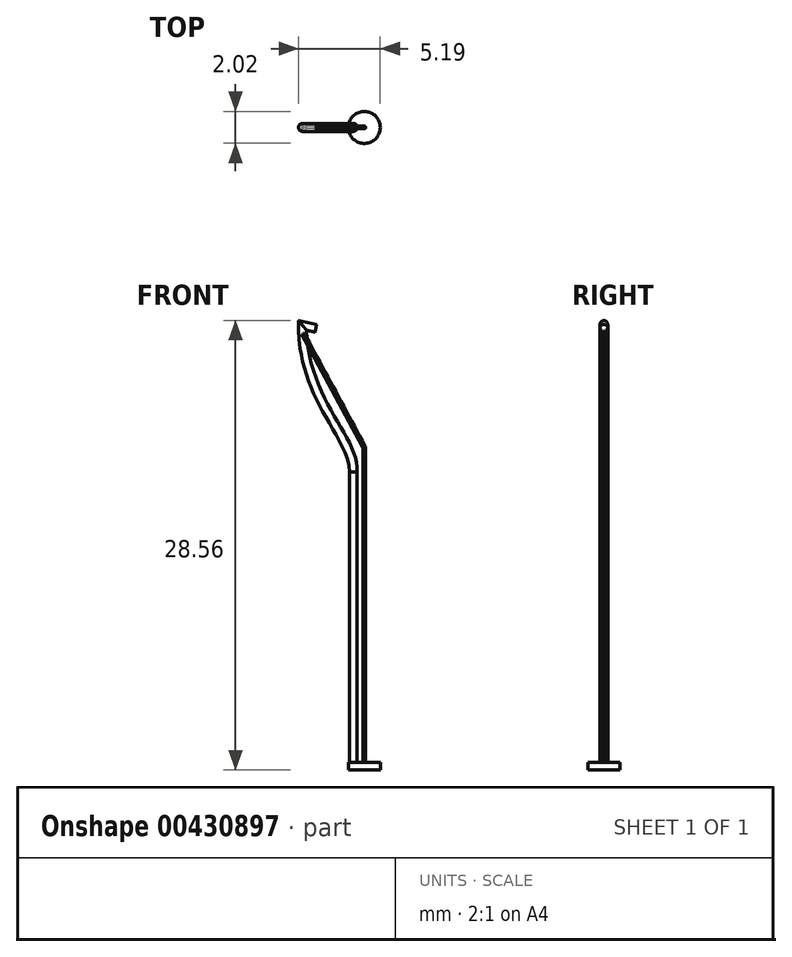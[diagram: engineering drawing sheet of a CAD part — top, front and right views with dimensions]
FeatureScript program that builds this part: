
annotation { "Feature Type Name" : "Feature", "Feature Type Description" : "" }
export const myFeature = defineFeature(function(context is Context, id is Id, definition is map)
    precondition{}
    {
        {
            var Q0;
            Q0=qCreatedBy(makeId("Front.planeOp"),FACE);
            var sketch = newSketch(context, id + "F0", { "sketchPlane" : qUnion([Q0])});
            skLineSegment(sketch, "E0", {"start": v(-0.7, 0) * mm, "end": v(-0.7, 18.43) * mm});
            skFitSpline(sketch, "E1", {"points": [v(-0.7, 18.43) * mm, v(-3.93, 27.75) * mm], "startDerivative": vector(0.31, 6.48) * mm, "endDerivative": vector(0.08, 13.97) * mm});
            skLineSegment(sketch, "E2", {"start": v(-3.93, 27.75) * mm, "end": v(-3.08, 27.56) * mm});
            skLineSegment(sketch, "E3", {"start": v(-3.93, 27.75) * mm, "end": v(-3.96, 23.1) * mm, "construction": true});
            skLineSegment(sketch, "E4", {"start": v(-0.7, 18.43) * mm, "end": v(-0.9, 18.43) * mm, "construction": true});
            skLineSegment(sketch, "E5", {"start": v(-0.9, 18.43) * mm, "end": v(-3.93, 27.75) * mm, "construction": true});
            skSolve(sketch);
        }
        {
            var Q0;
            Q0=qCreatedBy(makeId("Top.planeOp"),FACE);
            var sketch = newSketch(context, id + "F1", { "sketchPlane" : qUnion([Q0])});
            skCircle(sketch, "E6", {"center": v(-0.7, 0) * mm, "radius": 0.25 * mm});
            skSolve(sketch);
        }
        {
            var Q0;
            Q0 = qSketchRegion(id + "F1", true);
            var Q1;
            Q1 = qConstructionFilter(qBodyType(qCreatedBy(id + "F0" ,EDGE), BodyType.WIRE), ConstructionObject.NO);
            sweep(context, id + "F2", {"profiles" : qUnion([Q0]), "path" : qUnion([Q1])});
        }
        {
            var Q0;
            Q0=qCreatedBy(makeId("Top.planeOp"),FACE);
            var sketch = newSketch(context, id + "F3", { "sketchPlane" : qUnion([Q0])});
            skCircle(sketch, "E7", {"center": v(0, 0) * mm, "radius": 1.01 * mm});
            skSolve(sketch);
        }
        {
            var Q0;
            Q0 = qSketchRegion(id + "F3", true);
            extrude(context, id + "F4", {"entities" : qUnion([Q0]), "operationType" : NewBodyOperationType.ADD, "oppositeDirection" : true, "depth" : .5 * mm});
        }
        {
            var Q0;
            Q0=qCreatedBy(makeId("Front.planeOp"),FACE);
            var sketch = newSketch(context, id + "F5", { "sketchPlane" : qUnion([Q0])});
            skLineSegment(sketch, "E8", {"start": v(0, 0) * mm, "end": v(0, 19.94) * mm});
            skLineSegment(sketch, "E9", {"start": v(-3.9, 27.25) * mm, "end": v(-0.03, 20.06) * mm});
            skPoint(sketch, "E10.visualSharp", {"position": v(0, 20) * mm});
            skArc(sketch, "E10.filletArc", {"start": v(0, 19.94) * mm, "mid": v(0, 20) * mm, "end": v(-0.03, 20.06) * mm});
            skSolve(sketch);
        }
        {
            var Q0;
            Q0=makeQuery(id+"F4.opExtrude","CAP_FACE",FACE,{"disambiguationData":[OSD([sQuery(id+"F3.wireOp",EDGE,"E7")])],"isStart":true});
            var sketch = newSketch(context, id + "F6", { "sketchPlane" : qUnion([Q0])});
            skCircle(sketch, "E11", {"center": v(0, 0) * mm, "radius": 0.09 * mm});
            skSolve(sketch);
        }
        {
            var Q0;
            Q0=makeQuery(id+"F6.imprint","IMPRINT",FACE,{"disambiguationData":[TD([[makeQuery(id+"F6.imprint","IMPRINT",EDGE,{"derivedFrom":sQuery(id+"F6.wireOp",EDGE,"E11")}),1.0]])]});
            var Q1;
            Q1=sQuery(id+"F5.wireOp",EDGE,"E8");
            var Q2;
            Q2=sQuery(id+"F5.wireOp",EDGE,"E9");
            var Q3;
            Q3=sQuery(id+"F5.wireOp",EDGE,"E10.filletArc");
            sweep(context, id + "F7", {"profiles" : qUnion([Q0]), "path" : qUnion([Q1, Q2, Q3])});
        }
    });
